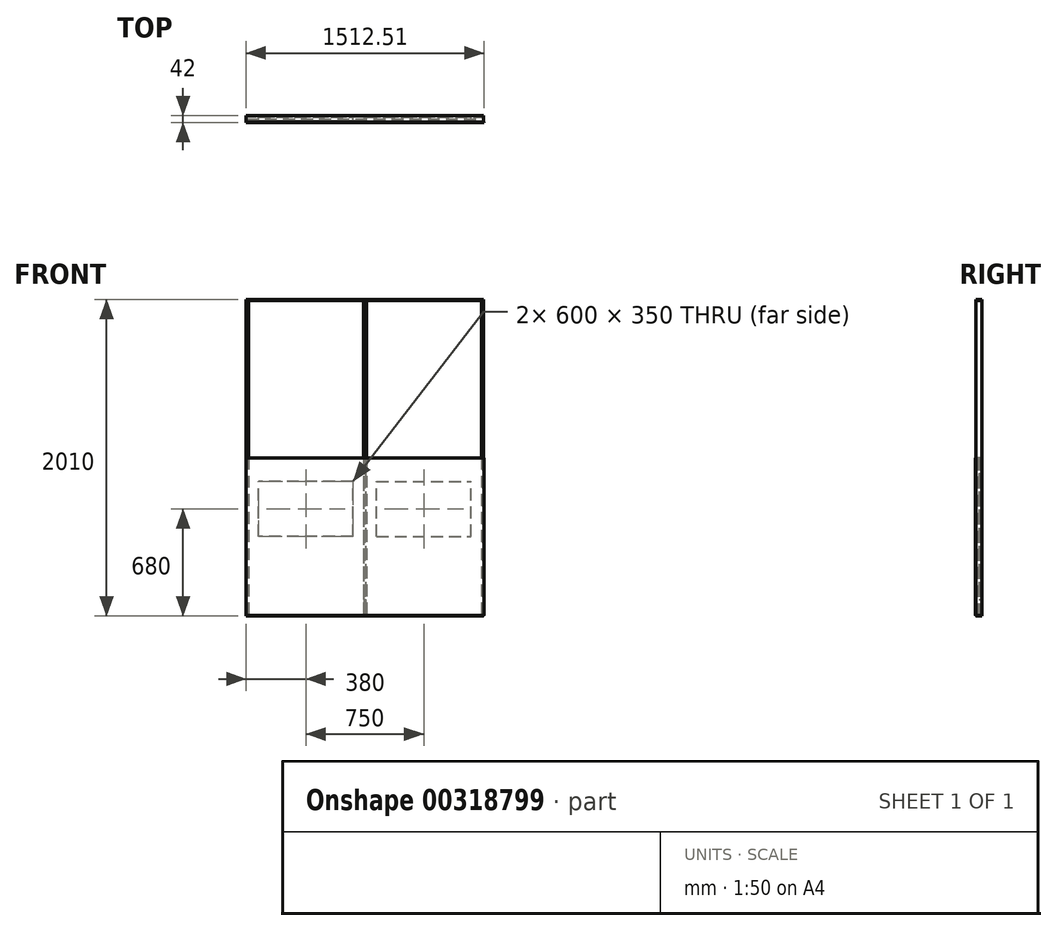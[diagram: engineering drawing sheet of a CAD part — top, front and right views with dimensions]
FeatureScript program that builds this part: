
annotation { "Feature Type Name" : "Feature", "Feature Type Description" : "" }
export const myFeature = defineFeature(function(context is Context, id is Id, definition is map)
    precondition{}
    {
        {
            var Q0;
            Q0=qCreatedBy(makeId("Top.planeOp"),FACE);
            var sketch = newSketch(context, id + "F0", { "sketchPlane" : qUnion([Q0])});
            skLineSegment(sketch, "E0", {"start": v(0, 0) * mm, "end": v(-750, 0) * mm, "construction": true});
            skLineSegment(sketch, "E1", {"start": v(-750, 0) * mm, "end": v(-750, -15) * mm});
            skLineSegment(sketch, "E2", {"start": v(-750, -15) * mm, "end": v(-740, -15) * mm});
            skLineSegment(sketch, "E3", {"start": v(-740, -15) * mm, "end": v(-740, -20) * mm});
            skLineSegment(sketch, "E4", {"start": v(-740, -20) * mm, "end": v(-755, -20) * mm});
            skLineSegment(sketch, "E5", {"start": v(-755, -20) * mm, "end": v(-755, 0) * mm});
            skLineSegment(sketch, "E6.MirrorCS", {"start": v(-740, 15) * mm, "end": v(-740, 20) * mm});
            skLineSegment(sketch, "E7.MirrorCS", {"start": v(-750, 15) * mm, "end": v(-740, 15) * mm});
            skLineSegment(sketch, "E8.MirrorCS", {"start": v(-750, 0) * mm, "end": v(-750, 15) * mm});
            skLineSegment(sketch, "E9.MirrorCS", {"start": v(-740, 20) * mm, "end": v(-755, 20) * mm});
            skLineSegment(sketch, "E10.MirrorCS", {"start": v(-755, 20) * mm, "end": v(-755, 0) * mm});
            skLineSegment(sketch, "E11.MirrorCS", {"start": v(740, -15) * mm, "end": v(740, -20) * mm});
            skLineSegment(sketch, "E12.MirrorCS", {"start": v(740, -20) * mm, "end": v(755, -20) * mm});
            skLineSegment(sketch, "E13.MirrorCS", {"start": v(755, -20) * mm, "end": v(755, 0) * mm});
            skLineSegment(sketch, "E14.MirrorCS", {"start": v(750, 0) * mm, "end": v(750, -15) * mm});
            skLineSegment(sketch, "E15.MirrorCS", {"start": v(750, -15) * mm, "end": v(740, -15) * mm});
            skLineSegment(sketch, "E16.MirrorCS", {"start": v(750, 15) * mm, "end": v(740, 15) * mm});
            skLineSegment(sketch, "E17.MirrorCS", {"start": v(750, 0) * mm, "end": v(750, 15) * mm});
            skLineSegment(sketch, "E18.MirrorCS", {"start": v(740, 15) * mm, "end": v(740, 20) * mm});
            skLineSegment(sketch, "E19.MirrorCS", {"start": v(740, 20) * mm, "end": v(755, 20) * mm});
            skLineSegment(sketch, "E20.MirrorCS", {"start": v(755, 20) * mm, "end": v(755, 0) * mm});
            skLineSegment(sketch, "E21.MirrorCS", {"start": v(0, 0) * mm, "end": v(750, 0) * mm, "construction": true});
            skLineSegment(sketch, "E22", {"start": v(-375, 79.86) * mm, "end": v(-375, -90.28) * mm, "construction": true});
            skLineSegment(sketch, "E23.MirrorCS", {"start": v(0, -15) * mm, "end": v(-10, -15) * mm});
            skLineSegment(sketch, "E24.MirrorCS", {"start": v(0, 0) * mm, "end": v(0, -15) * mm});
            skLineSegment(sketch, "E25.MirrorCS", {"start": v(-10, -15) * mm, "end": v(-10, -20) * mm});
            skLineSegment(sketch, "E26.MirrorCS", {"start": v(-10, 20) * mm, "end": v(5, 20) * mm});
            skLineSegment(sketch, "E27.MirrorCS", {"start": v(0, 15) * mm, "end": v(-10, 15) * mm});
            skLineSegment(sketch, "E28.MirrorCS", {"start": v(-10, 15) * mm, "end": v(-10, 20) * mm});
            skLineSegment(sketch, "E29.MirrorCS", {"start": v(0, 0) * mm, "end": v(0, 15) * mm});
            skLineSegment(sketch, "E30.MirrorCS", {"start": v(-10, -20) * mm, "end": v(5, -20) * mm});
            skLineSegment(sketch, "E31.MirrorCS", {"start": v(5, -20) * mm, "end": v(5, 0) * mm});
            skLineSegment(sketch, "E32.MirrorCS", {"start": v(5, 20) * mm, "end": v(5, 0) * mm});
            skLineSegment(sketch, "E33", {"start": v(375, 137.56) * mm, "end": v(375, -115.5) * mm, "construction": true});
            skLineSegment(sketch, "E34.MirrorCS", {"start": v(10, 15) * mm, "end": v(10, 20) * mm});
            skLineSegment(sketch, "E35.MirrorCS", {"start": v(0, 15) * mm, "end": v(10, 15) * mm});
            skLineSegment(sketch, "E36.MirrorCS", {"start": v(0, -15) * mm, "end": v(10, -15) * mm});
            skLineSegment(sketch, "E37.MirrorCS", {"start": v(10, 20) * mm, "end": v(-5, 20) * mm});
            skLineSegment(sketch, "E38.MirrorCS", {"start": v(10, -15) * mm, "end": v(10, -20) * mm});
            skLineSegment(sketch, "E39.MirrorCS", {"start": v(-5, 20) * mm, "end": v(-5, 0) * mm});
            skLineSegment(sketch, "E40.MirrorCS", {"start": v(10, -20) * mm, "end": v(-5, -20) * mm});
            skLineSegment(sketch, "E41.MirrorCS", {"start": v(-5, -20) * mm, "end": v(-5, 0) * mm});
            skSolve(sketch);
        }
        {
            var Q0;
            Q0=qSketchRegion(id+"F0",true);
            extrude(context, id + "F1", {"entities" : qUnion([Q0]), "depth" : 2000 * mm});
        }
        {
            var Q0;
            Q0=qCreatedBy(makeId("Front.planeOp"),FACE);
            var sketch = newSketch(context, id + "F2", { "sketchPlane" : qUnion([Q0])});
            skPoint(sketch, "E42.0", {"position": v(-750, 0) * mm});
            skLineSegment(sketch, "E43.bottom", {"start": v(-750, 0) * mm, "end": v(750, 0) * mm});
            skLineSegment(sketch, "E43.top", {"start": v(-750, 1000) * mm, "end": v(750, 1000) * mm});
            skLineSegment(sketch, "E43.left", {"start": v(-750, 0) * mm, "end": v(-750, 1000) * mm});
            skLineSegment(sketch, "E43.right", {"start": v(750, 0) * mm, "end": v(750, 1000) * mm});
            skSolve(sketch);
        }
        {
            var Q0;
            Q0=qSketchRegion(id+"F2",true);
            var Q1;
            Q1=makeQuery(id+"F2.imprint","IMPRINT",FACE,{"disambiguationData":[TD([[makeQuery(id+"F2.imprint","IMPRINT",EDGE,{"derivedFrom":sQuery(id+"F2.wireOp",EDGE,"E43.bottom")}),1.0]])]});
            extrude(context, id + "F3", {"entities" : qUnion([Q0, Q1]), "depth" : 15 * mm});
        }
        {
            var Q0;
            Q0=qSketchRegion(id+"F2",true);
            extrude(context, id + "F4", {"entities" : qUnion([Q0]), "oppositeDirection" : true, "depth" : 15 * mm});
        }
        {
            var Q0;
            Q0=makeQuery(id+"F1.opExtrude","CAP_FACE",FACE,{"disambiguationData":[OSD([sQuery(id+"F0.wireOp",EDGE,"E1"),sQuery(id+"F0.wireOp",EDGE,"E2"),sQuery(id+"F0.wireOp",EDGE,"E3"),sQuery(id+"F0.wireOp",EDGE,"E4"),sQuery(id+"F0.wireOp",EDGE,"E5"),sQuery(id+"F0.wireOp",EDGE,"E6.MirrorCS"),sQuery(id+"F0.wireOp",EDGE,"E7.MirrorCS"),sQuery(id+"F0.wireOp",EDGE,"E8.MirrorCS"),sQuery(id+"F0.wireOp",EDGE,"E9.MirrorCS"),sQuery(id+"F0.wireOp",EDGE,"E10.MirrorCS")])],"isStart":false});
            var sketch = newSketch(context, id + "F5", { "sketchPlane" : qUnion([Q0])});
            skLineSegment(sketch, "E44.bottom", {"start": v(-755, 20) * mm, "end": v(755, 20) * mm});
            skLineSegment(sketch, "E44.top", {"start": v(-755, -20) * mm, "end": v(755, -20) * mm});
            skLineSegment(sketch, "E44.left", {"start": v(-755, 20) * mm, "end": v(-755, -20) * mm});
            skLineSegment(sketch, "E44.right", {"start": v(755, 20) * mm, "end": v(755, -20) * mm});
            skLineSegment(sketch, "E45.MirrorCS", {"start": v(-755, -20) * mm, "end": v(-755, 20) * mm});
            skLineSegment(sketch, "E46.MirrorCS", {"start": v(755, -20) * mm, "end": v(755, 20) * mm});
            skSolve(sketch);
        }
        {
            var Q0;
            Q0=qSketchRegion(id+"F5",true);
            extrude(context, id + "F6", {"entities" : qUnion([Q0]), "depth" : 5 * mm});
        }
        {
            var Q0;
            Q0=makeQuery(id+"F0.imprint","IMPRINT",FACE,{"disambiguationData":[TD([[makeQuery(id+"F0.imprint","IMPRINT",EDGE,{"derivedFrom":sQuery(id+"F0.wireOp",EDGE,"E11.MirrorCS")}),1.0]])]});
            var sketch = newSketch(context, id + "F7", { "sketchPlane" : qUnion([Q0])});
            skLineSegment(sketch, "E47.bottom", {"start": v(755, 20) * mm, "end": v(-755, 20) * mm});
            skLineSegment(sketch, "E47.top", {"start": v(755, -20) * mm, "end": v(-755, -20) * mm});
            skLineSegment(sketch, "E47.left", {"start": v(755, 20) * mm, "end": v(755, -20) * mm});
            skLineSegment(sketch, "E47.right", {"start": v(-755, 20) * mm, "end": v(-755, -20) * mm});
            skSolve(sketch);
        }
        {
            var Q0;
            Q0=qSketchRegion(id+"F7",true);
            extrude(context, id + "F8", {"entities" : qUnion([Q0]), "oppositeDirection" : true, "depth" : 5 * mm});
        }
        {
            var Q0;
            Q0=makeQuery(id+"F4.opExtrude","CAP_FACE",FACE,{"disambiguationData":[OSD([sQuery(id+"F2.wireOp",EDGE,"E43.bottom"),sQuery(id+"F2.wireOp",EDGE,"E43.top"),sQuery(id+"F2.wireOp",EDGE,"E43.left"),sQuery(id+"F2.wireOp",EDGE,"E43.right")])],"isStart":false});
            var sketch = newSketch(context, id + "F9", { "sketchPlane" : qUnion([Q0])});
            skLineSegment(sketch, "E48", {"start": v(0, 100) * mm, "end": v(-600, 100) * mm});
            skLineSegment(sketch, "E49", {"start": v(-600, 100) * mm, "end": v(-600, 900) * mm});
            skLineSegment(sketch, "E50", {"start": v(-600, 900) * mm, "end": v(0, 900) * mm});
            skLineSegment(sketch, "E51.MirrorCS", {"start": v(600, 100) * mm, "end": v(600, 900) * mm});
            skLineSegment(sketch, "E52.MirrorCS", {"start": v(600, 900) * mm, "end": v(0, 900) * mm});
            skLineSegment(sketch, "E53.MirrorCS", {"start": v(0, 100) * mm, "end": v(600, 100) * mm});
            skSolve(sketch);
        }
        {
            var Q0;
            Q0=qSketchRegion(id+"F9",true);
            extrude(context, id + "F10", {"entities" : qUnion([Q0]), "operationType" : NewBodyOperationType.REMOVE, "oppositeDirection" : true, "depth" : 15 * mm});
        }
        {
            var Q0;
            Q0=makeQuery(id+"F4.opExtrude","CAP_FACE",FACE,{"disambiguationData":[OSD([sQuery(id+"F2.wireOp",EDGE,"E43.bottom"),sQuery(id+"F2.wireOp",EDGE,"E43.top"),sQuery(id+"F2.wireOp",EDGE,"E43.left"),sQuery(id+"F2.wireOp",EDGE,"E43.right")])],"isStart":false});
            var sketch = newSketch(context, id + "F11", { "sketchPlane" : qUnion([Q0])});
            skLineSegment(sketch, "E54.bottom", {"start": v(-600, 900) * mm, "end": v(600, 900) * mm});
            skLineSegment(sketch, "E54.top", {"start": v(-600, 100) * mm, "end": v(600, 100) * mm});
            skLineSegment(sketch, "E54.left", {"start": v(-600, 900) * mm, "end": v(-600, 100) * mm});
            skLineSegment(sketch, "E54.right", {"start": v(600, 900) * mm, "end": v(600, 100) * mm});
            skSolve(sketch);
        }
        {
            var Q0;
            Q0=qSketchRegion(id+"F11",true);
            extrude(context, id + "F12", {"entities" : qUnion([Q0]), "oppositeDirection" : true, "depth" : 15 * mm});
        }
        {
            var Q0;
            Q0=makeQuery(id+"F4.opExtrude","SWEPT_BODY",BODY,{"disambiguationData":[OSD([sQuery(id+"F2.wireOp",EDGE,"E43.bottom"),sQuery(id+"F2.wireOp",EDGE,"E43.top"),sQuery(id+"F2.wireOp",EDGE,"E43.left"),sQuery(id+"F2.wireOp",EDGE,"E43.right")])]});
            deleteBodies(context, id + "F13", {"entities" : qUnion([Q0])});
        }
        {
            var Q0;
            Q0=makeQuery(id+"F12.opExtrude","SWEPT_BODY",BODY,{"disambiguationData":[OSD([sQuery(id+"F11.wireOp",EDGE,"E54.bottom"),sQuery(id+"F11.wireOp",EDGE,"E54.top"),sQuery(id+"F11.wireOp",EDGE,"E54.left"),sQuery(id+"F11.wireOp",EDGE,"E54.right")])]});
            deleteBodies(context, id + "F14", {"entities" : qUnion([Q0])});
        }
        {
            var Q0;
            Q0=makeQuery(id+"F3.opExtrude","CAP_FACE",FACE,{"disambiguationData":[OSD([sQuery(id+"F2.wireOp",EDGE,"E43.bottom"),sQuery(id+"F2.wireOp",EDGE,"E43.top"),sQuery(id+"F2.wireOp",EDGE,"E43.left"),sQuery(id+"F2.wireOp",EDGE,"E43.right")])],"isStart":true});
            var sketch = newSketch(context, id + "F15", { "sketchPlane" : qUnion([Q0])});
            skLineSegment(sketch, "E55.bottom", {"start": v(-750, 0) * mm, "end": v(0, 0) * mm});
            skLineSegment(sketch, "E55.top", {"start": v(-750, 1000) * mm, "end": v(0, 1000) * mm});
            skLineSegment(sketch, "E55.left", {"start": v(-750, 0) * mm, "end": v(-750, 1000) * mm});
            skLineSegment(sketch, "E55.right", {"start": v(0, 0) * mm, "end": v(0, 1000) * mm});
            skLineSegment(sketch, "E56.bottom", {"start": v(-675, 850) * mm, "end": v(-75, 850) * mm});
            skLineSegment(sketch, "E56.top", {"start": v(-675, 500) * mm, "end": v(-75, 500) * mm});
            skLineSegment(sketch, "E56.left", {"start": v(-675, 850) * mm, "end": v(-675, 500) * mm});
            skLineSegment(sketch, "E56.right", {"start": v(-75, 850) * mm, "end": v(-75, 500) * mm});
            skLineSegment(sketch, "E57.MirrorCS", {"start": v(750, 1000) * mm, "end": v(0, 1000) * mm});
            skLineSegment(sketch, "E58.MirrorCS", {"start": v(75, 850) * mm, "end": v(75, 500) * mm});
            skLineSegment(sketch, "E59.MirrorCS", {"start": v(675, 850) * mm, "end": v(675, 500) * mm});
            skLineSegment(sketch, "E60.MirrorCS", {"start": v(675, 500) * mm, "end": v(75, 500) * mm});
            skLineSegment(sketch, "E61.MirrorCS", {"start": v(675, 850) * mm, "end": v(75, 850) * mm});
            skSolve(sketch);
        }
        {
            var Q0;
            Q0=makeQuery(id+"F15.imprint","IMPRINT",FACE,{"disambiguationData":[TD([[makeQuery(id+"F15.imprint","IMPRINT",EDGE,{"derivedFrom":sQuery(id+"F15.wireOp",EDGE,"E55.bottom")}),-1.0]])]});
            extrude(context, id + "F16", {"entities" : qUnion([Q0]), "endBound" : BoundingType.SYMMETRIC, "depth" : 25 * mm});
        }
        {
            var Q0;
            Q0=makeQuery(id+"F16.opExtrude","SWEPT_BODY",BODY,{"disambiguationData":[OSD([sQuery(id+"F15.wireOp",EDGE,"E55.bottom"),sQuery(id+"F15.wireOp",EDGE,"E55.top"),sQuery(id+"F15.wireOp",EDGE,"E55.left"),sQuery(id+"F15.wireOp",EDGE,"E55.right"),sQuery(id+"F15.wireOp",EDGE,"E56.bottom"),sQuery(id+"F15.wireOp",EDGE,"E56.top"),sQuery(id+"F15.wireOp",EDGE,"E56.left"),sQuery(id+"F15.wireOp",EDGE,"E56.right")])]});
            var Q1;
            Q1=qCreatedBy(makeId("Right.planeOp"),FACE);
            mirror(context, id + "F17", {"entities" : qUnion([Q0]), "mirrorPlane" : qUnion([Q1])});
        }
        {
            var Q0;
            Q0=makeQuery(id+"F16.opExtrude","CAP_FACE",FACE,{"disambiguationData":[OSD([sQuery(id+"F15.wireOp",EDGE,"E55.bottom"),sQuery(id+"F15.wireOp",EDGE,"E55.top"),sQuery(id+"F15.wireOp",EDGE,"E55.left"),sQuery(id+"F15.wireOp",EDGE,"E55.right"),sQuery(id+"F15.wireOp",EDGE,"E56.bottom"),sQuery(id+"F15.wireOp",EDGE,"E56.top"),sQuery(id+"F15.wireOp",EDGE,"E56.left"),sQuery(id+"F15.wireOp",EDGE,"E56.right")])],"isStart":false});
            var sketch = newSketch(context, id + "F18", { "sketchPlane" : qUnion([Q0])});
            skLineSegment(sketch, "E62.bottom", {"start": v(-675, 850) * mm, "end": v(-75, 850) * mm});
            skLineSegment(sketch, "E62.top", {"start": v(-675, 500) * mm, "end": v(-75, 500) * mm});
            skLineSegment(sketch, "E62.left", {"start": v(-675, 850) * mm, "end": v(-675, 500) * mm});
            skLineSegment(sketch, "E62.right", {"start": v(-75, 850) * mm, "end": v(-75, 500) * mm});
            skSolve(sketch);
        }
        {
            var Q0;
            Q0=makeQuery(id+"F18.imprint","IMPRINT",FACE,{"disambiguationData":[TD([[makeQuery(id+"F18.imprint","IMPRINT",EDGE,{"derivedFrom":sQuery(id+"F18.wireOp",EDGE,"E62.bottom")}),-1.0]])]});
            var Q1;
            Q1=makeQuery(id+"F16.opExtrude","CAP_FACE",FACE,{"disambiguationData":[OSD([sQuery(id+"F15.wireOp",EDGE,"E55.bottom"),sQuery(id+"F15.wireOp",EDGE,"E55.top"),sQuery(id+"F15.wireOp",EDGE,"E55.left"),sQuery(id+"F15.wireOp",EDGE,"E55.right"),sQuery(id+"F15.wireOp",EDGE,"E56.bottom"),sQuery(id+"F15.wireOp",EDGE,"E56.top"),sQuery(id+"F15.wireOp",EDGE,"E56.left"),sQuery(id+"F15.wireOp",EDGE,"E56.right")])],"isStart":true});
            extrude(context, id + "F19", {"entities" : qUnion([Q0]), "endBound" : BoundingType.UP_TO_SURFACE, "oppositeDirection" : true, "endBoundEntityFace" : qUnion([Q1]), "depth" : 25 * mm});
        }
        {
            var Q0;
            Q0=makeQuery(id+"F19.opExtrude","SWEPT_BODY",BODY,{"disambiguationData":[OSD([sQuery(id+"F18.wireOp",EDGE,"E62.bottom"),sQuery(id+"F18.wireOp",EDGE,"E62.top"),sQuery(id+"F18.wireOp",EDGE,"E62.left"),sQuery(id+"F18.wireOp",EDGE,"E62.right")])]});
            var Q1;
            Q1=qCreatedBy(makeId("Right.planeOp"),FACE);
            mirror(context, id + "F20", {"entities" : qUnion([Q0]), "mirrorPlane" : qUnion([Q1])});
        }
        {
            var Q0;
            Q0=makeQuery(id+"F1.opExtrude","SWEPT_FACE",FACE,{"disambiguationData":[OSD([sQuery(id+"F0.wireOp",EDGE,"E4")])]});
            var sketch = newSketch(context, id + "F21", { "sketchPlane" : qUnion([Q0])});
            skLineSegment(sketch, "E63.bottom", {"start": v(757.51, 0) * mm, "end": v(-755, 0) * mm});
            skLineSegment(sketch, "E63.top", {"start": v(757.51, 1000) * mm, "end": v(-755, 1000) * mm});
            skLineSegment(sketch, "E63.left", {"start": v(757.51, 0) * mm, "end": v(757.51, 1000) * mm});
            skLineSegment(sketch, "E63.right", {"start": v(-755, 0) * mm, "end": v(-755, 1000) * mm});
            skSolve(sketch);
        }
        {
            var Q0;
            Q0 = qSketchRegion(id + "F21", true);
            extrude(context, id + "F22", {"entities" : qUnion([Q0]), "depth" : 2 * mm});
        }
    });
